# Revit family: Shower-VALVE-KOHLER-CYCLING_VALVE-K-11737T_1
name_source: partatom
category: Plumbing Fixtures
revit_build: Autodesk Revit 2017 (Build: 20160225_1515(x64)
units: mm (PartAtom-declared; Revit-internal decimal feet)

## family parameters
Cut with Voids When Loaded = No
Host = Face
OmniClass Number = 23.27.31.00
OmniClass Title = Valves
Part Type = Normal
Room Calculation Point = No
Round Connector Dimension = Use Diameter
Shared = No

## types (2) — shared parameters
ADA Compliant = No
Assembly Code = D2020
CW Connection = Yes
Cold Water Inlet = Cold Water Inlet
Date Modified = 02/25/2021
Default Elevation = 36"
Description = W/40MM CARTRIDGE&DIVETER
Flow Rate = 0 GPM
HW Connection = Yes
Height = 6 1/8"
Hot Water Inlet = Hot Water Inlet
Hot Water Outlet 1 = Tempered Water Outlet 1
Hot Water Outlet 2 = Tempered Water Outlet 2
Length = 5 3/8"
Manufacturer = KOHLER Co.
Master Format 2014 = 23 09 13.33
Master Format 2014 Name = Control Valves
Material = Brass Construction
Pressure = 0.00 psi
Product Name = CYCLING VALVE
URL = http://www.kohler.com.cn
Vent Connection = No
Waste Connection = No
Waste Water Outlet = Waste Water Outlet
WaterSense Certified = No
Width = 2 13/16"

## per-type parameters (varying)
| type | Finish | Model | Type |
| CP-Polished Chrome | Kohler-Metal-CP-Polished_Chrome | K-11737T-CP | 1 |
| RGD-Rose Gold | Kohler-Metal-RGD-Rose_Gold | K-11737T-RGD | 2 |

## geometry (parser evidence)
native form markers: Sweep x4
no freeform markers — native parametric forms only
